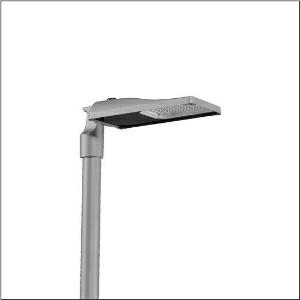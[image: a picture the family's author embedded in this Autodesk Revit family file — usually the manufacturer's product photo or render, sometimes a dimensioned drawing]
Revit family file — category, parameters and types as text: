
# Revit family: streetlight_sl_31_mini___st1_0a_5xh2d3as08ga_13ac
name_source: partatom
category: Lighting Fixtures
units: mm (PartAtom-declared; Revit-internal decimal feet)

## family parameters
Cut with Voids When Loaded = No
Host = Face
Light Source = No
Part Type = Normal
Room Calculation Point = No
Round Connector Dimension = Use Diameter
Shared = No

## types (1)
- --- (1 x LED, 5880 lm, 39.3 W, 3000K)
    Apparent Load = 39 VA
    CIE Flux Codes = 37 72 97 100 100
    Color Rendering = 70
    Color Temperature = 3000K
    Default Elevation = 1800 mm
    Description = Streetlight SL 31 mini D4i mast luminaire for post-top, side-entry; light control with lens of PMMA; light distribution: ST1.0a, direct asymmetric distribution, for standard-compliant lighting for roads and squares; LED: luminous flux: 5.880lm, light colour: 730, colour temperature: 3000K; luminous efficacy: 149,6lm/W; control: pre-setting: logarithmic dimming characteristic, flexible luminous flux parameterisation, time-dependent luminous flux control, constant luminous flux control, power reduction, intelligent temperature release in ECG and LED module, overheat protection; luminaire housing, of diecast aluminium, SITECO metallic grey (DB 702S), corrosivity category C5 high according to DIN EN ISO 12944; cover of toughened safety glass, transparent, mast flange of diecast aluminium, SITECO metallic grey (DB 702S), spigot size: 76/60mm, mast flange included unmounted; cable length: 8,5m, connection cable pre-assembled; mains connection: 220..240V, AC, 50/60Hz; power consumption (at start of service life): 39,3W / (at end of service life): 40,7W / (with reduced operation 50%): 18,1W; protection rating (complete): IP66; insulation class (complete): insulation class II (safety insulation); impact resistance: IK10; certification: CE, ENEC, ENEC+, VDE, UKCA, ZD4i; permissible operating ambient temperature for outdoor applications: -40..+50°C; packaging unit: 1 piece

Light Distribution: ST1.0a
    Height = 76 mm
    Lamp = 1 x LED
    Lamp Light Flux = 5880 lm
    Lamp Power = 39.3 W
    Lamp count = 1
    Length = 547 mm
    Luminous efficacy = 150 lm/W
    Manufacturer = Siteco
    ModVariant = No
    Model = 5XH2D3AS08GA
    Number of Poles = 1
    OnlyDefault = Yes
    Power Factor = 1
    Product Name = Streetlight SL 31 mini | ST1.0a
    Product group = mast luminaire | pylon top
    ProductGroupID = 6100
    Protection Class = Protection class II
    Protection Degree = IP 66
    RLX_Detail_Level = 1
    RLX_Emergency_Light_Flux = 0 lm
    RLX_Emergency_Type = 0
    RLX_Emergency_Type_DB = No
    RlxData = <blob elided: 39721 chars, md5=8d1caff4>
    Socket = socket
    Standby Power = 0 W
    System Light Flux = 5880 lm
    System Power = 39 W
    Type Comments = factory setting: luminous flux: 100 % | dim-lin: 254 | 798 mA
    Type Image = l_1300330.jpg
    URL = http://relux.com
    VarID = @adj_061453
    Voltage = 0 V
    Weight = 0.00 kg
    Width = 265 mm

## geometry (parser evidence)
native form markers: Blend x4, Sweep x9
no freeform markers — native parametric forms only
